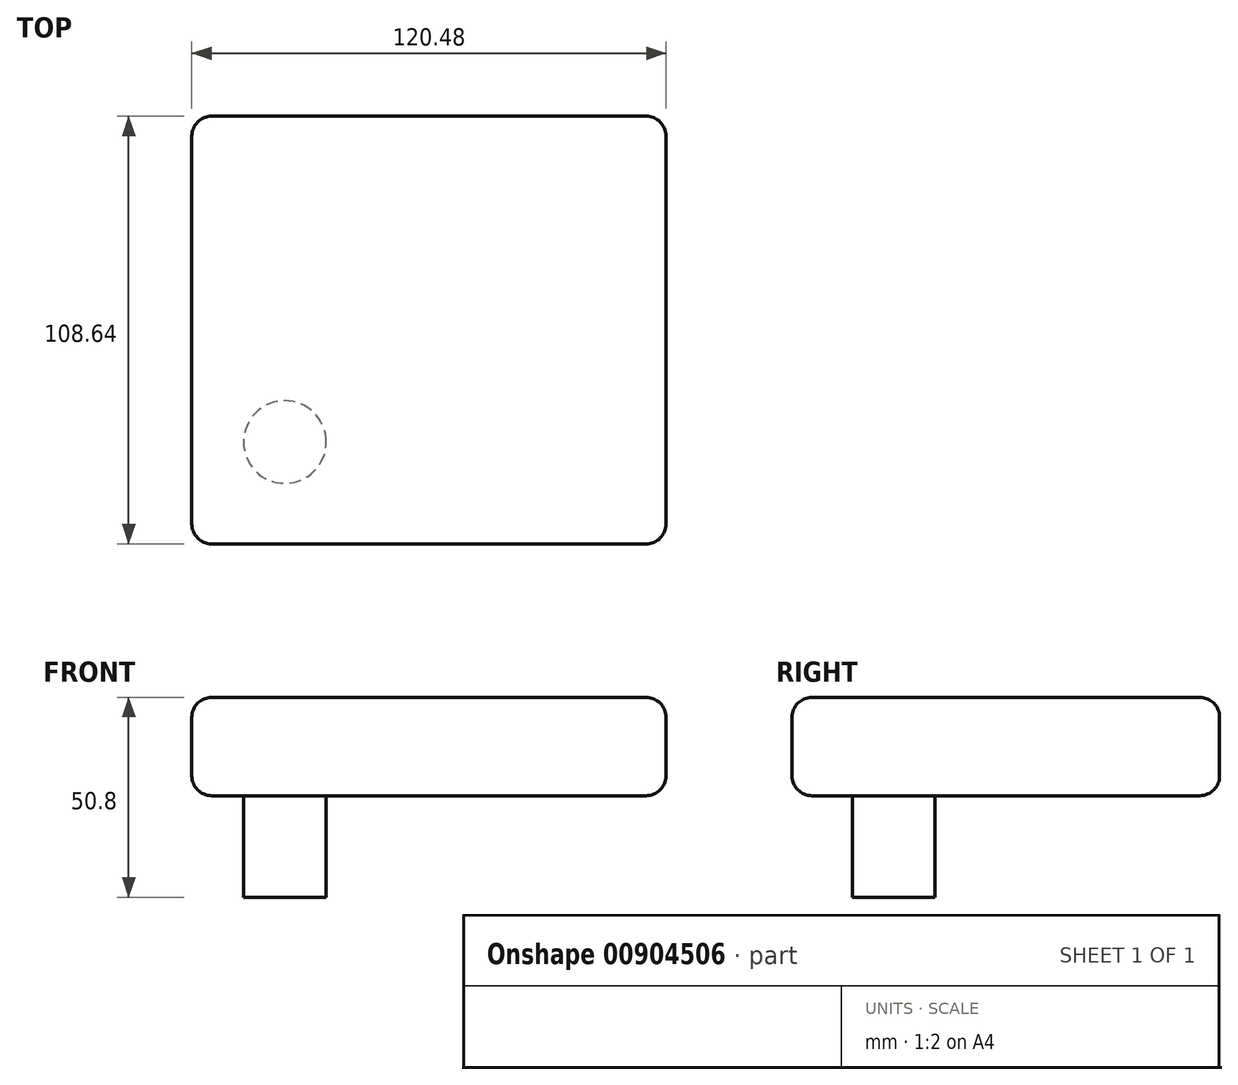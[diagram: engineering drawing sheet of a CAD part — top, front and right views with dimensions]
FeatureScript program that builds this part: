
annotation { "Feature Type Name" : "Feature", "Feature Type Description" : "" }
export const myFeature = defineFeature(function(context is Context, id is Id, definition is map)
    precondition{}
    {
        {
            var Q0;
            Q0=qCreatedBy(makeId("Top.planeOp"),FACE);
            var sketch = newSketch(context, id + "F0", { "sketchPlane" : qUnion([Q0])});
            skLineSegment(sketch, "E0.bottom", {"start": v(-60.24, 54.32) * mm, "end": v(60.24, 54.32) * mm});
            skLineSegment(sketch, "E0.top", {"start": v(-60.24, -54.32) * mm, "end": v(60.24, -54.32) * mm});
            skLineSegment(sketch, "E0.left", {"start": v(-60.24, 54.32) * mm, "end": v(-60.24, -54.32) * mm});
            skLineSegment(sketch, "E0.right", {"start": v(60.24, 54.32) * mm, "end": v(60.24, -54.32) * mm});
            skPoint(sketch, "E0.middle", {"position": v(0, 0) * mm});
            skSolve(sketch);
        }
        {
            var Q0;
            Q0=makeQuery(id+"F0.imprint","IMPRINT",FACE,{"disambiguationData":[TD([[makeQuery(id+"F0.imprint","IMPRINT",EDGE,{"derivedFrom":sQuery(id+"F0.wireOp",EDGE,"E0.bottom")}),-1.0]])]});
            extrude(context, id + "F1", {"entities" : qUnion([Q0]), "oppositeDirection" : true, "depth" : 25 * mm, "offsetDistance" : 25.4 * mm});
        }
        {
            var Q0;
            Q0=makeQuery(id+"F1.opExtrude","CAP_FACE",FACE,{"disambiguationData":[OSD([sQuery(id+"F0.wireOp",EDGE,"E0.bottom"),sQuery(id+"F0.wireOp",EDGE,"E0.top"),sQuery(id+"F0.wireOp",EDGE,"E0.left"),sQuery(id+"F0.wireOp",EDGE,"E0.right")])],"isStart":true});
            var sketch = newSketch(context, id + "F2", { "sketchPlane" : qUnion([Q0])});
            skCircle(sketch, "E1", {"center": v(-36.59, 28.46) * mm, "radius": 10.5 * mm});
            skCircle(sketch, "E2.MirrorC", {"center": v(36.59, 28.46) * mm, "radius": 10.5 * mm, "construction": true});
            skCircle(sketch, "E3.MirrorC", {"center": v(-36.59, -28.46) * mm, "radius": 10.5 * mm});
            skCircle(sketch, "E4.MirrorC", {"center": v(36.59, -28.46) * mm, "radius": 10.5 * mm});
            skCircle(sketch, "E5.MirrorC", {"center": v(36.59, 28.46) * mm, "radius": 10.5 * mm});
            skSolve(sketch);
        }
        {
            var Q0;
            Q0=makeQuery(id+"F1.opExtrude","CAP_EDGE",EDGE,{"disambiguationData":[OSD([sQuery(id+"F0.wireOp",EDGE,"E0.top")])],"isStart":false});
            var Q1;
            Q1=makeQuery(id+"F1.opExtrude","CAP_EDGE",EDGE,{"disambiguationData":[OSD([sQuery(id+"F0.wireOp",EDGE,"E0.left")])],"isStart":false});
            var Q2;
            Q2=makeQuery(id+"F1.opExtrude","CAP_EDGE",EDGE,{"disambiguationData":[OSD([sQuery(id+"F0.wireOp",EDGE,"E0.bottom")])],"isStart":false});
            var Q3;
            Q3=makeQuery(id+"F1.opExtrude","CAP_EDGE",EDGE,{"disambiguationData":[OSD([sQuery(id+"F0.wireOp",EDGE,"E0.right")])],"isStart":false});
            var Q4;
            Q4=makeQuery(id+"F1.opExtrude","SWEPT_EDGE",EDGE,{"disambiguationData":[OSD([sQuery(id+"F0.wireOp",EDGE,"E0.top"),sQuery(id+"F0.wireOp",EDGE,"E0.right")])]});
            var Q5;
            Q5=makeQuery(id+"F1.opExtrude","CAP_EDGE",EDGE,{"disambiguationData":[OSD([sQuery(id+"F0.wireOp",EDGE,"E0.right")])],"isStart":true});
            var Q6;
            Q6=makeQuery(id+"F1.opExtrude","SWEPT_EDGE",EDGE,{"disambiguationData":[OSD([sQuery(id+"F0.wireOp",EDGE,"E0.bottom"),sQuery(id+"F0.wireOp",EDGE,"E0.right")])]});
            var Q7;
            Q7=makeQuery(id+"F1.opExtrude","SWEPT_EDGE",EDGE,{"disambiguationData":[OSD([sQuery(id+"F0.wireOp",EDGE,"E0.top"),sQuery(id+"F0.wireOp",EDGE,"E0.left")])]});
            var Q8;
            Q8=makeQuery(id+"F1.opExtrude","CAP_EDGE",EDGE,{"disambiguationData":[OSD([sQuery(id+"F0.wireOp",EDGE,"E0.top")])],"isStart":true});
            var Q9;
            Q9=makeQuery(id+"F1.opExtrude","CAP_EDGE",EDGE,{"disambiguationData":[OSD([sQuery(id+"F0.wireOp",EDGE,"E0.left")])],"isStart":true});
            var Q10;
            Q10=makeQuery(id+"F1.opExtrude","CAP_EDGE",EDGE,{"disambiguationData":[OSD([sQuery(id+"F0.wireOp",EDGE,"E0.bottom")])],"isStart":true});
            var Q11;
            Q11=makeQuery(id+"F1.opExtrude","SWEPT_EDGE",EDGE,{"disambiguationData":[OSD([sQuery(id+"F0.wireOp",EDGE,"E0.bottom"),sQuery(id+"F0.wireOp",EDGE,"E0.left")])]});
            var Q12;
            Q12=makeQuery(id+"F1.opExtrude","CAP_FACE",FACE,{"disambiguationData":[OSD([sQuery(id+"F0.wireOp",EDGE,"E0.bottom"),sQuery(id+"F0.wireOp",EDGE,"E0.top"),sQuery(id+"F0.wireOp",EDGE,"E0.left"),sQuery(id+"F0.wireOp",EDGE,"E0.right")])],"isStart":true});
            fillet(context, id + "F3", {"entities" : qUnion([Q0, Q1, Q2, Q3, Q4, Q5, Q6, Q7, Q8, Q9, Q10, Q11, Q12]), "radius" : 5.08 * mm, "tangentPropagation" : true, "allowEdgeOverflow" : false});
        }
        {
            var Q0;
            Q0=makeQuery(id+"F2.imprint","IMPRINT",FACE,{"disambiguationData":[TD([[makeQuery(id+"F2.imprint","IMPRINT",EDGE,{"derivedFrom":sQuery(id+"F2.wireOp",EDGE,"E3.MirrorC")}),1.0]])]});
            extrude(context, id + "F4", {"entities" : qUnion([Q0]), "operationType" : NewBodyOperationType.ADD, "oppositeDirection" : true, "depth" : 25.4 * mm, "offsetDistance" : 25.4 * mm});
        }
        {
            var Q0;
            Q0=makeQuery(id+"F4.opExtrude","CAP_FACE",FACE,{"disambiguationData":[OSD([sQuery(id+"F0.wireOp",EDGE,"E0.bottom"),sQuery(id+"F0.wireOp",EDGE,"E0.top"),sQuery(id+"F0.wireOp",EDGE,"E0.left"),sQuery(id+"F0.wireOp",EDGE,"E0.right"),sQuery(id+"F2.wireOp",EDGE,"E3.MirrorC"),sQuery(id+"F2.wireOp",EDGE,"E1"),sQuery(id+"F2.wireOp",EDGE,"E4.MirrorC"),sQuery(id+"F2.wireOp",EDGE,"E5.MirrorC")])],"isStart":false});
            extrude(context, id + "F5", {"entities" : qUnion([Q0]), "operationType" : NewBodyOperationType.ADD, "depth" : 25.4 * mm, "offsetDistance" : 25.4 * mm});
        }
    });
